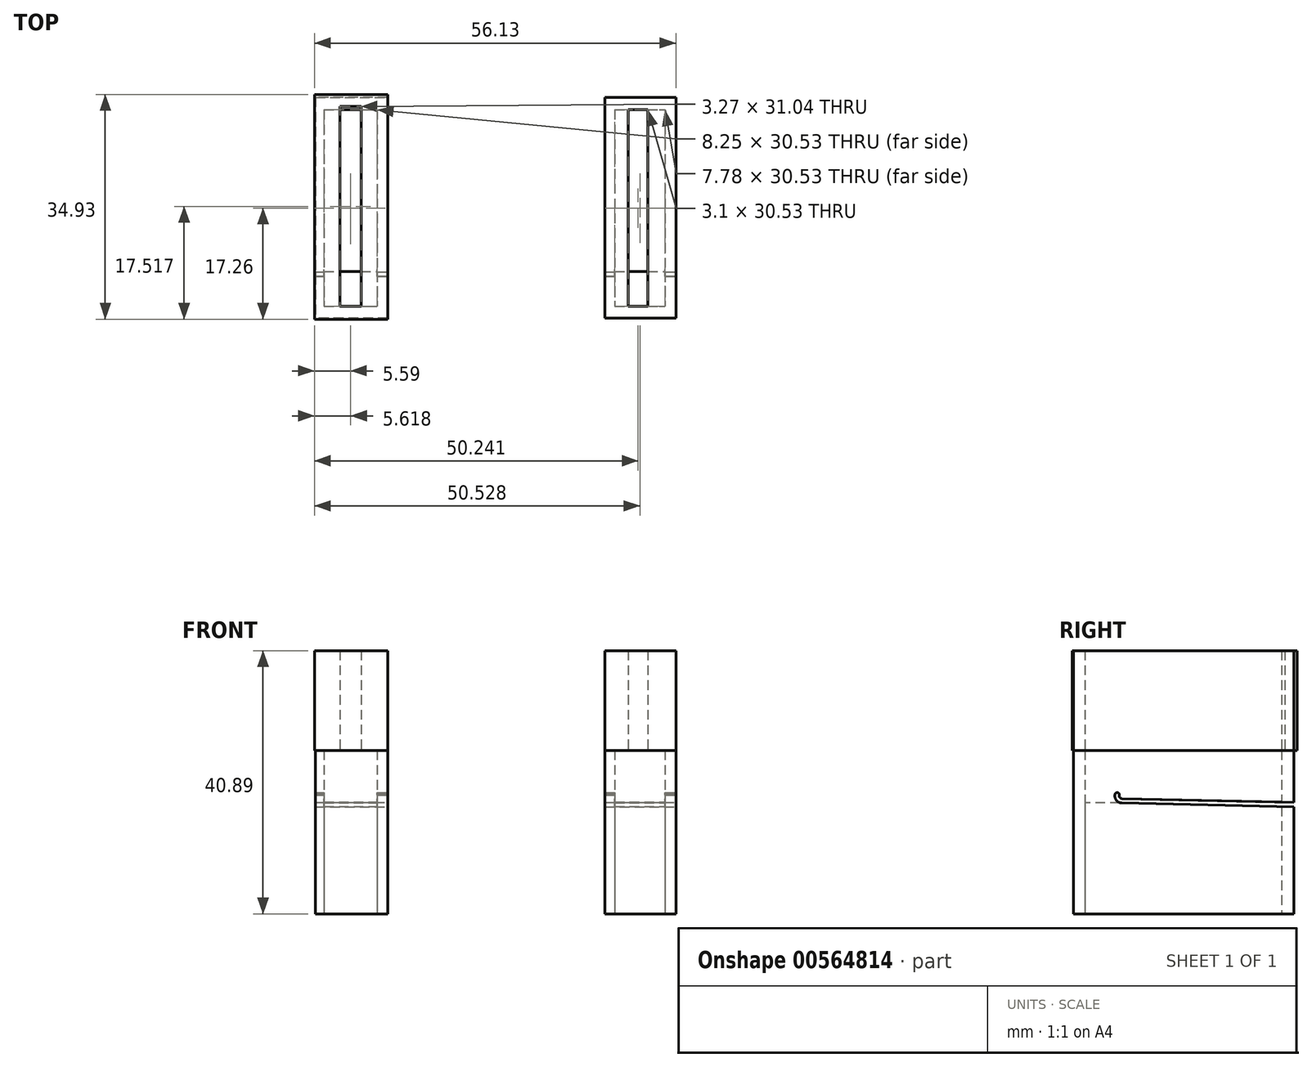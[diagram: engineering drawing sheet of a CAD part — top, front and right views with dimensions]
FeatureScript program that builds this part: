
annotation { "Feature Type Name" : "Feature", "Feature Type Description" : "" }
export const myFeature = defineFeature(function(context is Context, id is Id, definition is map)
    precondition{}
    {
        {
            var Q0;
            Q0=qCreatedBy(makeId("Top.planeOp"),FACE);
            var sketch = newSketch(context, id + "F0", { "sketchPlane" : qUnion([Q0])});
            skLineSegment(sketch, "E0.bottom", {"start": v(-10.05, 22.25) * mm, "end": v(0.97, 22.25) * mm});
            skLineSegment(sketch, "E0.top", {"start": v(-10.05, -12.03) * mm, "end": v(0.97, -12.03) * mm});
            skLineSegment(sketch, "E0.left", {"start": v(-10.05, 22.25) * mm, "end": v(-10.05, -12.03) * mm});
            skLineSegment(sketch, "E0.right", {"start": v(0.97, 22.25) * mm, "end": v(0.97, -12.03) * mm});
            skLineSegment(sketch, "E1.bottom", {"start": v(-43.75, 22.25) * mm, "end": v(-55.02, 22.25) * mm});
            skLineSegment(sketch, "E1.top", {"start": v(-43.75, -12.03) * mm, "end": v(-55.02, -12.03) * mm});
            skLineSegment(sketch, "E1.left", {"start": v(-43.75, 22.25) * mm, "end": v(-43.75, -12.03) * mm});
            skLineSegment(sketch, "E1.right", {"start": v(-55.02, 22.25) * mm, "end": v(-55.02, -12.03) * mm});
            skLineSegment(sketch, "E2.bottom", {"start": v(-53.67, 20.3) * mm, "end": v(-45.42, 20.3) * mm});
            skLineSegment(sketch, "E2.top", {"start": v(-53.67, -10.23) * mm, "end": v(-45.42, -10.23) * mm});
            skLineSegment(sketch, "E2.left", {"start": v(-53.67, 20.3) * mm, "end": v(-53.67, -10.23) * mm});
            skLineSegment(sketch, "E2.right", {"start": v(-45.42, 20.3) * mm, "end": v(-45.42, -10.23) * mm});
            skLineSegment(sketch, "E3.bottom", {"start": v(-8.52, 20.3) * mm, "end": v(-0.74, 20.3) * mm});
            skLineSegment(sketch, "E3.top", {"start": v(-8.52, -10.23) * mm, "end": v(-0.74, -10.23) * mm});
            skLineSegment(sketch, "E3.left", {"start": v(-8.52, 20.3) * mm, "end": v(-8.52, -10.23) * mm});
            skLineSegment(sketch, "E3.right", {"start": v(-0.74, 20.3) * mm, "end": v(-0.74, -10.23) * mm});
            skSolve(sketch);
        }
        {
            var Q0;
            Q0=makeQuery(id+"F0.imprint","IMPRINT",FACE,{"disambiguationData":[TD([[makeQuery(id+"F0.imprint","IMPRINT",EDGE,{"derivedFrom":sQuery(id+"F0.wireOp",EDGE,"E1.bottom")}),1.0]])]});
            var Q1;
            Q1=makeQuery(id+"F0.imprint","IMPRINT",FACE,{"disambiguationData":[TD([[makeQuery(id+"F0.imprint","IMPRINT",EDGE,{"derivedFrom":sQuery(id+"F0.wireOp",EDGE,"E0.bottom")}),-1.0]])]});
            extrude(context, id + "F1", {"entities" : qUnion([Q0, Q1]), "depth" : 25.4 * mm, "offsetDistance" : 25.4 * mm});
        }
        {
            var Q0;
            Q0=makeQuery(id+"F0.imprint","IMPRINT",FACE,{"disambiguationData":[TD([[makeQuery(id+"F0.imprint","IMPRINT",EDGE,{"derivedFrom":sQuery(id+"F0.wireOp",EDGE,"E3.bottom")}),-1.0]])]});
            var Q1;
            Q1=makeQuery(id+"F0.imprint","IMPRINT",FACE,{"disambiguationData":[TD([[makeQuery(id+"F0.imprint","IMPRINT",EDGE,{"derivedFrom":sQuery(id+"F0.wireOp",EDGE,"E2.bottom")}),-1.0]])]});
            extrude(context, id + "F2", {"entities" : qUnion([Q0, Q1]), "depth" : 17.27 * mm, "offsetDistance" : 25.4 * mm});
        }
        {
            var Q0;
            Q0=makeQuery(id+"F1.opExtrude","CAP_FACE",FACE,{"disambiguationData":[OSD([sQuery(id+"F0.wireOp",EDGE,"E0.bottom"),sQuery(id+"F0.wireOp",EDGE,"E0.top"),sQuery(id+"F0.wireOp",EDGE,"E0.left"),sQuery(id+"F0.wireOp",EDGE,"E0.right"),sQuery(id+"F0.wireOp",EDGE,"E3.bottom"),sQuery(id+"F0.wireOp",EDGE,"E3.top"),sQuery(id+"F0.wireOp",EDGE,"E3.left"),sQuery(id+"F0.wireOp",EDGE,"E3.right")])],"isStart":false});
            var sketch = newSketch(context, id + "F3", { "sketchPlane" : qUnion([Q0])});
            skLineSegment(sketch, "E4.bottom", {"start": v(-55.16, 22.71) * mm, "end": v(-43.8, 22.71) * mm});
            skLineSegment(sketch, "E4.top", {"start": v(-55.16, -12.22) * mm, "end": v(-43.8, -12.22) * mm});
            skLineSegment(sketch, "E4.left", {"start": v(-55.16, 22.71) * mm, "end": v(-55.16, -12.22) * mm});
            skLineSegment(sketch, "E4.right", {"start": v(-43.8, 22.71) * mm, "end": v(-43.8, -12.22) * mm});
            skLineSegment(sketch, "E5.bottom", {"start": v(-10.05, 22.25) * mm, "end": v(0.97, 22.25) * mm});
            skLineSegment(sketch, "E5.top", {"start": v(-10.05, -12.03) * mm, "end": v(0.97, -12.03) * mm});
            skLineSegment(sketch, "E5.left", {"start": v(-10.05, 22.25) * mm, "end": v(-10.05, -12.03) * mm});
            skLineSegment(sketch, "E5.right", {"start": v(0.97, 22.25) * mm, "end": v(0.97, -12.03) * mm});
            skLineSegment(sketch, "E6.bottom", {"start": v(-51.2, 20.82) * mm, "end": v(-47.94, 20.82) * mm});
            skLineSegment(sketch, "E6.top", {"start": v(-51.2, -10.23) * mm, "end": v(-47.94, -10.23) * mm});
            skLineSegment(sketch, "E6.left", {"start": v(-51.2, 20.82) * mm, "end": v(-51.2, -10.23) * mm});
            skLineSegment(sketch, "E6.right", {"start": v(-47.94, 20.82) * mm, "end": v(-47.94, -10.23) * mm});
            skLineSegment(sketch, "E7.bottom", {"start": v(-6.47, 20.3) * mm, "end": v(-3.37, 20.3) * mm});
            skLineSegment(sketch, "E7.top", {"start": v(-6.47, -10.23) * mm, "end": v(-3.37, -10.23) * mm});
            skLineSegment(sketch, "E7.left", {"start": v(-6.47, 20.3) * mm, "end": v(-6.47, -10.23) * mm});
            skLineSegment(sketch, "E7.right", {"start": v(-3.37, 20.3) * mm, "end": v(-3.37, -10.23) * mm});
            skSolve(sketch);
        }
        {
            var Q0;
            {var subQ0=sQuery(id+"F3.wireOp",EDGE,"E7.right");Q0=makeQuery(id+"F3.imprint","IMPRINT",FACE,{"disambiguationData":[TD([[makeQuery(id+"F3.imprint","IMPRINT",EDGE,{"derivedFrom":subQ0}),1.0]])]});}
            var Q1;
            {var subQ0=sQuery(id+"F3.wireOp",EDGE,"E7.left");Q1=makeQuery(id+"F3.imprint","IMPRINT",FACE,{"disambiguationData":[TD([[makeQuery(id+"F3.imprint","IMPRINT",EDGE,{"derivedFrom":subQ0}),-1.0]])]});}
            var Q2;
            Q2=makeQuery(id+"F3.imprint","IMPRINT",FACE,{"disambiguationData":[TD([[makeQuery(id+"F3.imprint","IMPRINT",EDGE,{"derivedFrom":sQuery(id+"F3.wireOp",EDGE,"E4.bottom")}),-1.0]])]});
            var Q3;
            Q3=makeQuery(id+"F3.imprint","IMPRINT",FACE,{"disambiguationData":[TD([[makeQuery(id+"F3.imprint","IMPRINT",EDGE,{"derivedFrom":sQuery(id+"F3.wireOp",EDGE,"E5.bottom")}),-1.0]])]});
            extrude(context, id + "F4", {"entities" : qUnion([Q0, Q1, Q2, Q3]), "depth" : 15.5 * mm, "offsetDistance" : 25.4 * mm});
        }
        {
            var Q0;
            Q0=makeQuery(id+"F1.opExtrude","SWEPT_FACE",FACE,{"disambiguationData":[OSD([sQuery(id+"F0.wireOp",EDGE,"E0.right")])]});
            var sketch = newSketch(context, id + "F5", { "sketchPlane" : qUnion([Q0])});
            skLineSegment(sketch, "E8", {"start": v(22.25, 16.64) * mm, "end": v(-4.51, 17.23) * mm});
            skArc(sketch, "E9", {"start": v(-5.52, 18.68) * mm, "mid": v(-5.39, 17.7) * mm, "end": v(-4.51, 17.23) * mm});
            skLineSegment(sketch, "E10.0", {"start": v(22.26, 17.32) * mm, "end": v(-4.5, 17.91) * mm});
            skArc(sketch, "E10.1", {"start": v(-4.87, 18.45) * mm, "mid": v(-4.82, 18.09) * mm, "end": v(-4.5, 17.91) * mm});
            skArc(sketch, "E11", {"start": v(-4.87, 18.45) * mm, "mid": v(-5.1, 18.82) * mm, "end": v(-5.52, 18.68) * mm});
            skLineSegment(sketch, "E12", {"start": v(22.26, 17.32) * mm, "end": v(22.25, 16.64) * mm});
            skSolve(sketch);
        }
        {
            var Q0;
            {var subQ4=sQuery(id+"F5.wireOp",EDGE,"E8");Q0=makeQuery(id+"F5.imprint","IMPRINT",FACE,{"disambiguationData":[TD([[makeQuery(id+"F5.imprint","IMPRINT",EDGE,{"derivedFrom":subQ4}),-1.0]])]});}
            extrude(context, id + "F6", {"entities" : qUnion([Q0]), "operationType" : NewBodyOperationType.REMOVE, "oppositeDirection" : true, "depth" : 59.18 * mm, "offsetDistance" : 25.4 * mm});
        }
    });
